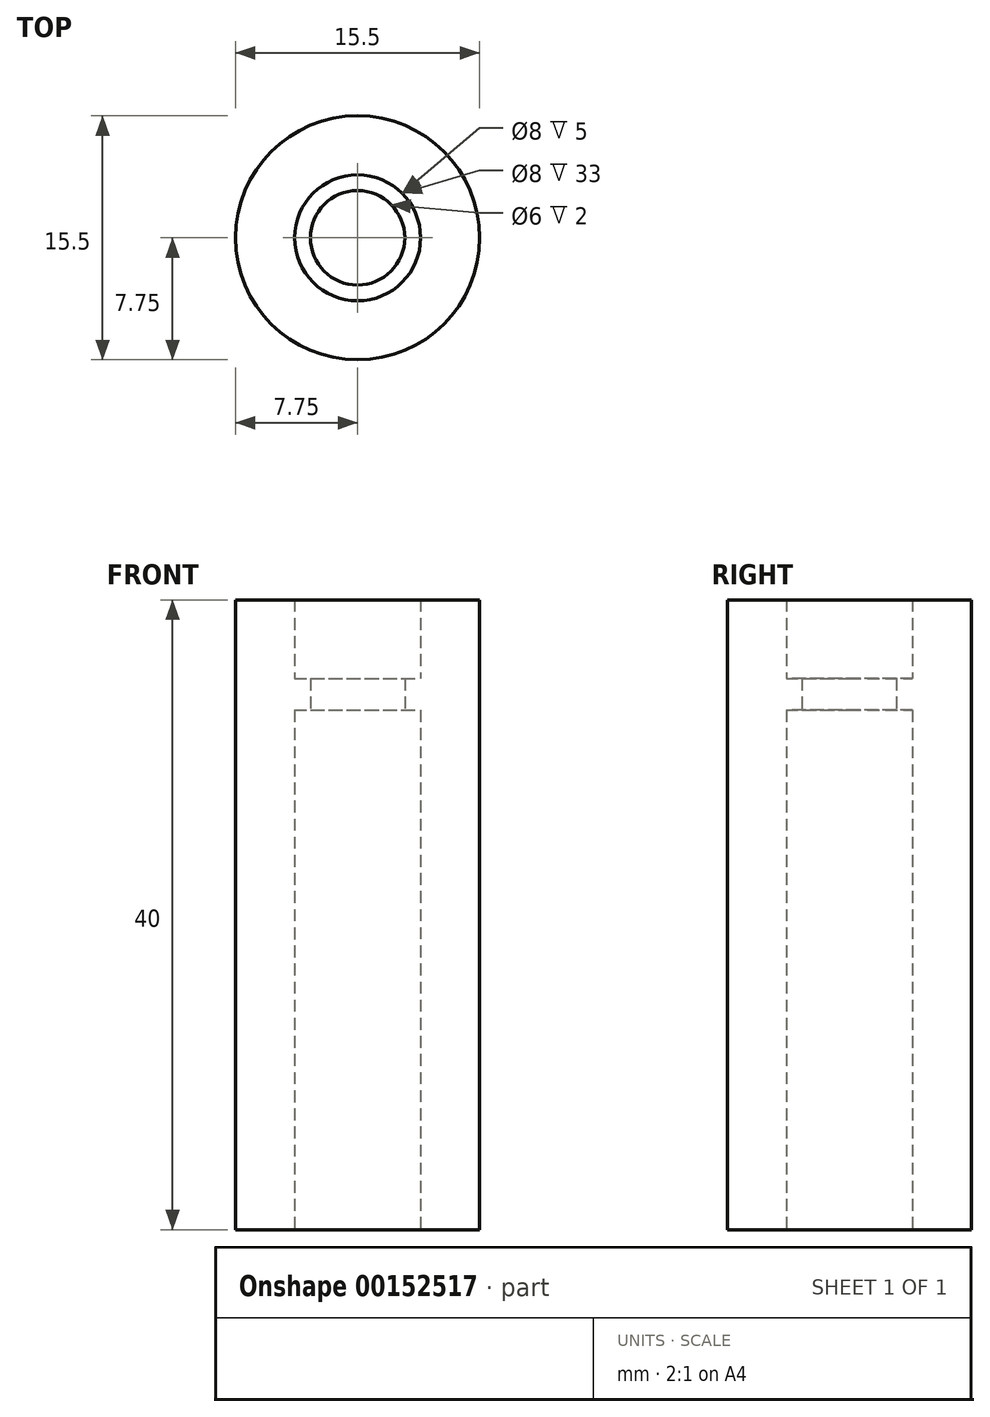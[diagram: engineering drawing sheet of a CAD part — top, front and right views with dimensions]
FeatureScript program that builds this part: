
annotation { "Feature Type Name" : "Feature", "Feature Type Description" : "" }
export const myFeature = defineFeature(function(context is Context, id is Id, definition is map)
    precondition{}
    {
        {
            var Q0;
            Q0=qCreatedBy(makeId("Right.planeOp"),FACE);
            var sketch = newSketch(context, id + "F0", { "sketchPlane" : qUnion([Q0])});
            skLineSegment(sketch, "E0.bottom", {"start": v(0, 0) * mm, "end": v(-7.75, 0) * mm});
            skLineSegment(sketch, "E0.top", {"start": v(0, 40) * mm, "end": v(-7.75, 40) * mm});
            skLineSegment(sketch, "E0.left", {"start": v(0, 0) * mm, "end": v(0, 40) * mm});
            skLineSegment(sketch, "E0.right", {"start": v(-7.75, 0) * mm, "end": v(-7.75, 40) * mm});
            skLineSegment(sketch, "E1.bottom", {"start": v(0, 0) * mm, "end": v(-4, 0) * mm});
            skLineSegment(sketch, "E1.top", {"start": v(0, 40) * mm, "end": v(-4, 40) * mm});
            skLineSegment(sketch, "E1.right", {"start": v(-4, 0) * mm, "end": v(-4, 40) * mm});
            skLineSegment(sketch, "E2.bottom", {"start": v(-4, 35) * mm, "end": v(-3, 35) * mm});
            skLineSegment(sketch, "E2.top", {"start": v(-4, 33) * mm, "end": v(-3, 33) * mm});
            skLineSegment(sketch, "E2.left", {"start": v(-4, 35) * mm, "end": v(-4, 33) * mm});
            skLineSegment(sketch, "E2.right", {"start": v(-3, 35) * mm, "end": v(-3, 33) * mm});
            skSolve(sketch);
        }
        {
            var Q0;
            Q0=makeQuery(id+"F0.imprint","IMPRINT",FACE,{"disambiguationData":[TD([[makeQuery(id+"F0.imprint","IMPRINT",EDGE,{"derivedFrom":sQuery(id+"F0.wireOp",EDGE,"E2.bottom")}),-1.0]])]});
            var Q1;
            {var subQ1=sQuery(id+"F0.wireOp",EDGE,"E0.bottom");Q1=makeQuery(id+"F0.imprint","IMPRINT",FACE,{"disambiguationData":[TD([[makeQuery(id+"F0.imprint","IMPRINT",EDGE,{"derivedFrom":subQ1}),-1.0]])]});}
            var Q2;
            Q2=sQuery(id+"F0.wireOp",EDGE,"E0.left");
            revolve(context, id + "F1", {"entities" : qUnion([Q0, Q1]), "axis" : qUnion([Q2]), "revolveType" : RevolveType.FULL});
        }
    });
